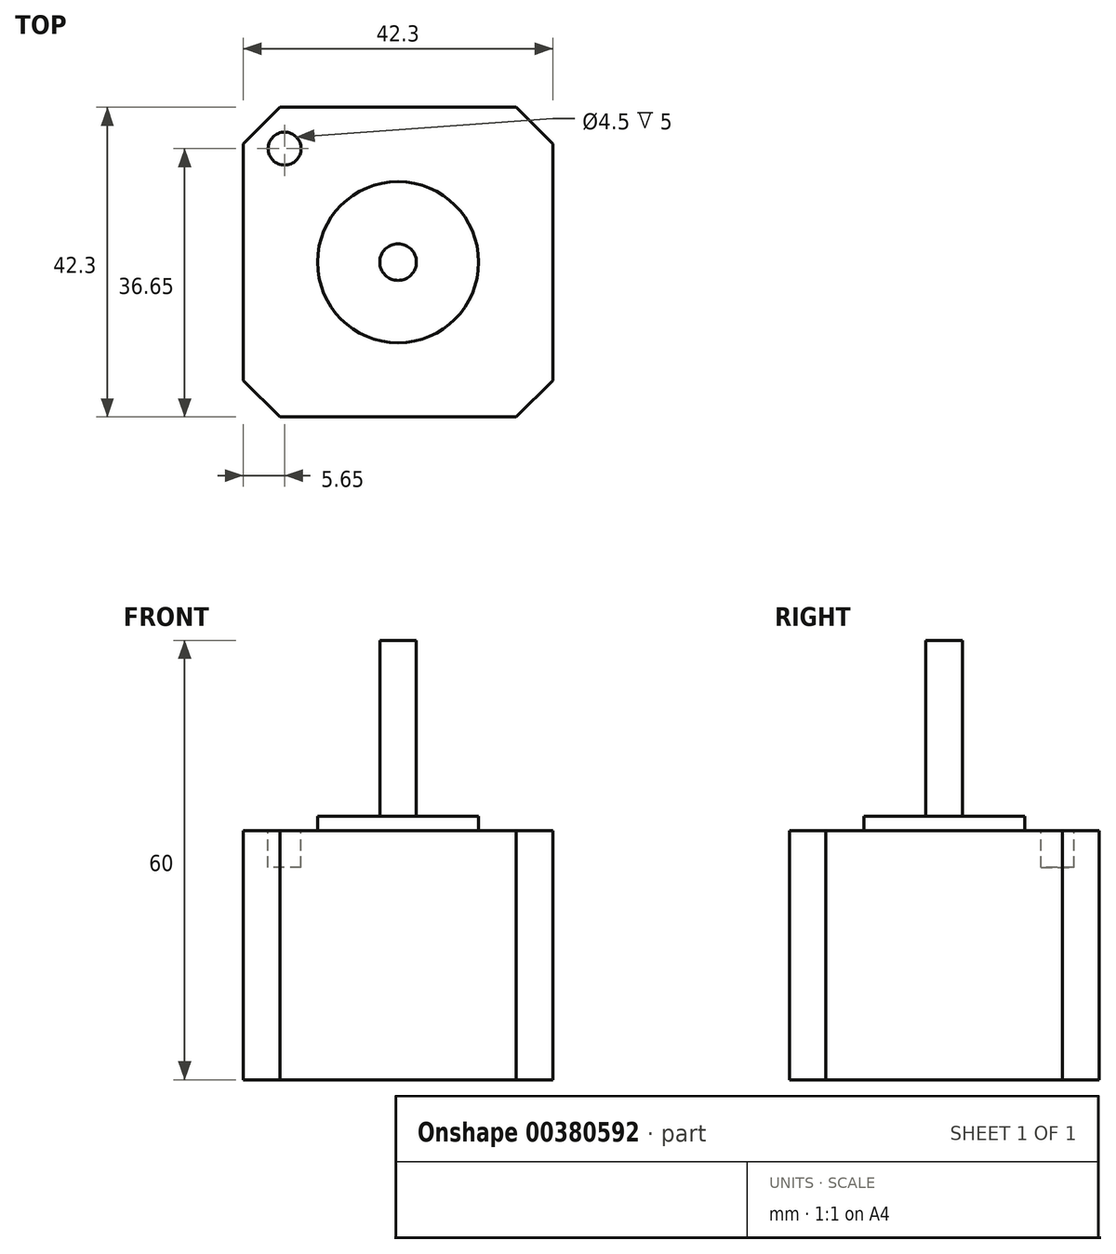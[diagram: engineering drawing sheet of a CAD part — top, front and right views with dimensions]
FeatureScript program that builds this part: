
annotation { "Feature Type Name" : "Feature", "Feature Type Description" : "" }
export const myFeature = defineFeature(function(context is Context, id is Id, definition is map)
    precondition{}
    {
        {
            var Q0;
            Q0=qCreatedBy(makeId("Top.planeOp"),FACE);
            var sketch = newSketch(context, id + "F0", { "sketchPlane" : qUnion([Q0])});
            skLineSegment(sketch, "E0.bottom", {"start": v(21.15, -21.15) * mm, "end": v(-21.15, -21.15) * mm});
            skLineSegment(sketch, "E0.top", {"start": v(21.15, 21.15) * mm, "end": v(-21.15, 21.15) * mm});
            skLineSegment(sketch, "E0.left", {"start": v(21.15, -21.15) * mm, "end": v(21.15, 21.15) * mm});
            skLineSegment(sketch, "E0.right", {"start": v(-21.15, -21.15) * mm, "end": v(-21.15, 21.15) * mm});
            skPoint(sketch, "E0.middle", {"position": v(0, 0) * mm});
            skSolve(sketch);
        }
        {
            var Q0;
            Q0 = qSketchRegion(id + "F0", true);
            extrude(context, id + "F1", {"entities" : qUnion([Q0]), "depth" : 34 * mm});
        }
        {
            var Q0;
            Q0=makeQuery(id+"F1.opExtrude","CAP_FACE",FACE,{"disambiguationData":[OSD([sQuery(id+"F0.wireOp",EDGE,"E0.bottom"),sQuery(id+"F0.wireOp",EDGE,"E0.top"),sQuery(id+"F0.wireOp",EDGE,"E0.left"),sQuery(id+"F0.wireOp",EDGE,"E0.right")])],"isStart":false});
            var sketch = newSketch(context, id + "F2", { "sketchPlane" : qUnion([Q0])});
            skCircle(sketch, "E1", {"center": v(0, 0) * mm, "radius": 11 * mm});
            skSolve(sketch);
        }
        {
            var Q0;
            Q0 = qSketchRegion(id + "F2", true);
            extrude(context, id + "F3", {"entities" : qUnion([Q0]), "operationType" : NewBodyOperationType.ADD, "depth" : 2 * mm});
        }
        {
            var Q0;
            Q0=makeQuery(id+"F3.opExtrude","CAP_FACE",FACE,{"disambiguationData":[OSD([sQuery(id+"F2.wireOp",EDGE,"E1")])],"isStart":false});
            var sketch = newSketch(context, id + "F4", { "sketchPlane" : qUnion([Q0])});
            skCircle(sketch, "E2", {"center": v(0, 0) * mm, "radius": 2.5 * mm});
            skSolve(sketch);
        }
        {
            var Q0;
            Q0 = qSketchRegion(id + "F4", true);
            extrude(context, id + "F5", {"entities" : qUnion([Q0]), "operationType" : NewBodyOperationType.ADD, "depth" : 24 * mm});
        }
        {
            var Q0;
            Q0=makeQuery(id+"F1.opExtrude","CAP_FACE",FACE,{"disambiguationData":[OSD([sQuery(id+"F0.wireOp",EDGE,"E0.bottom"),sQuery(id+"F0.wireOp",EDGE,"E0.top"),sQuery(id+"F0.wireOp",EDGE,"E0.left"),sQuery(id+"F0.wireOp",EDGE,"E0.right")])],"isStart":false});
            var sketch = newSketch(context, id + "F6", { "sketchPlane" : qUnion([Q0])});
            skCircle(sketch, "E3", {"center": v(-15.5, 15.5) * mm, "radius": 2.25 * mm});
            skSolve(sketch);
        }
        {
            var Q0;
            Q0 = qSketchRegion(id + "F6", true);
            extrude(context, id + "F7", {"entities" : qUnion([Q0]), "operationType" : NewBodyOperationType.REMOVE, "oppositeDirection" : true, "depth" : 5 * mm});
        }
        {
            var Q0;
            Q0=makeQuery(id+"F1.opExtrude","SWEPT_EDGE",EDGE,{"disambiguationData":[OSD([sQuery(id+"F0.wireOp",EDGE,"E0.bottom"),sQuery(id+"F0.wireOp",EDGE,"E0.right")])]});
            var Q1;
            Q1=makeQuery(id+"F1.opExtrude","SWEPT_EDGE",EDGE,{"disambiguationData":[OSD([sQuery(id+"F0.wireOp",EDGE,"E0.top"),sQuery(id+"F0.wireOp",EDGE,"E0.right")])]});
            var Q2;
            Q2=makeQuery(id+"F1.opExtrude","SWEPT_EDGE",EDGE,{"disambiguationData":[OSD([sQuery(id+"F0.wireOp",EDGE,"E0.top"),sQuery(id+"F0.wireOp",EDGE,"E0.left")])]});
            var Q3;
            Q3=makeQuery(id+"F1.opExtrude","SWEPT_EDGE",EDGE,{"disambiguationData":[OSD([sQuery(id+"F0.wireOp",EDGE,"E0.bottom"),sQuery(id+"F0.wireOp",EDGE,"E0.left")])]});
            chamfer(context, id + "F8", {"entities" : qUnion([Q0, Q1, Q2, Q3]), "width" : 5 * mm, "tangentPropagation" : true});
        }
    });
